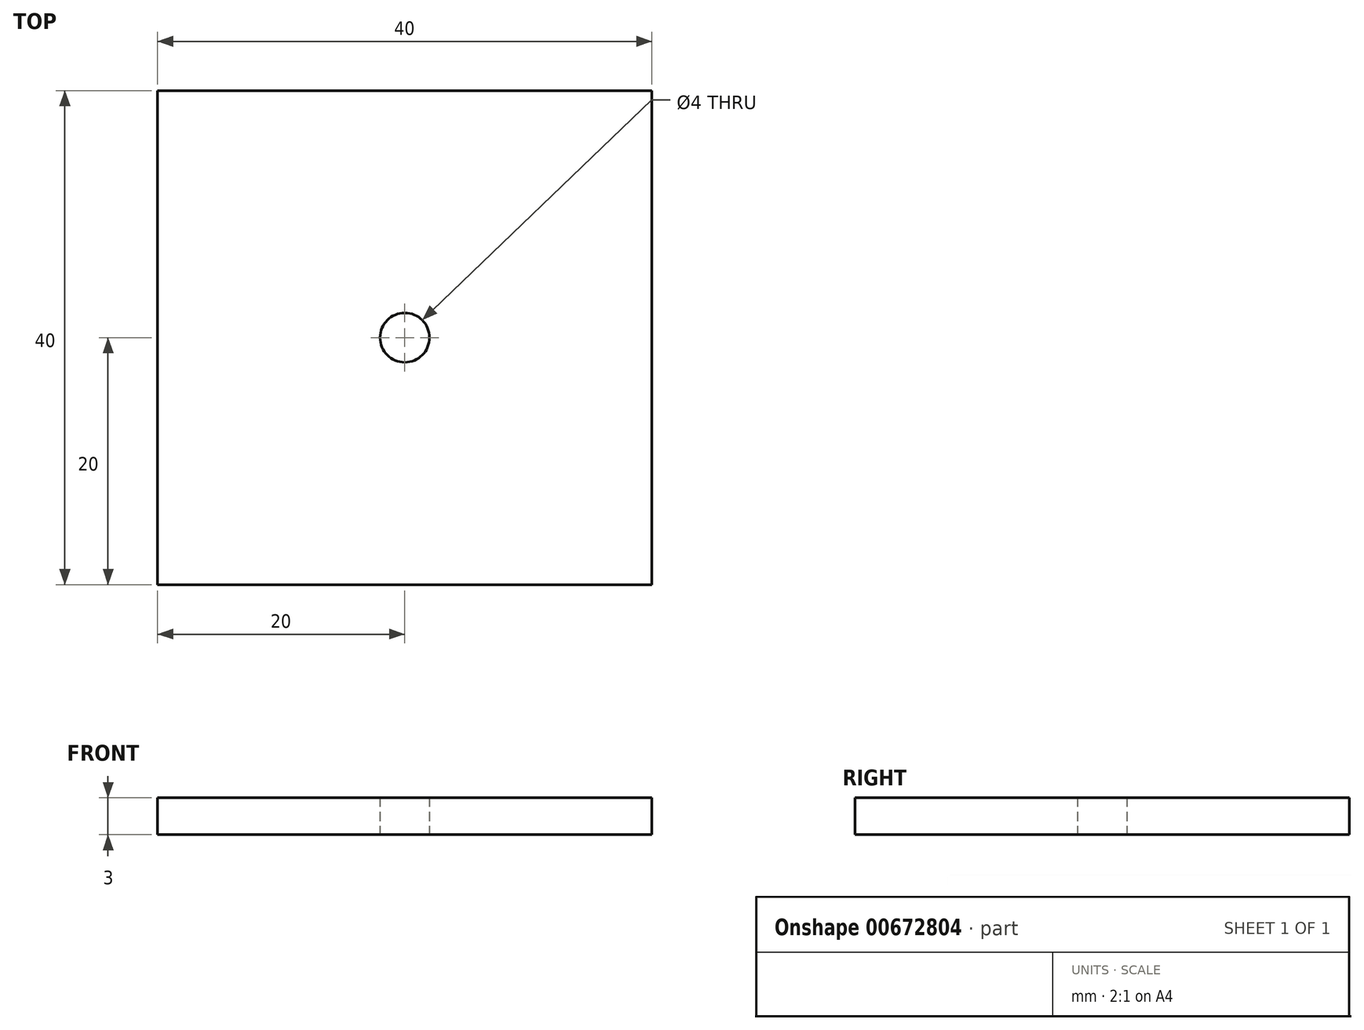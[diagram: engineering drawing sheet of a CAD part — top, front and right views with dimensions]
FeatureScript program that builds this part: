
annotation { "Feature Type Name" : "Feature", "Feature Type Description" : "" }
export const myFeature = defineFeature(function(context is Context, id is Id, definition is map)
    precondition{}
    {
        {
            var Q0;
            Q0=qCreatedBy(makeId("Top.planeOp"),FACE);
            var sketch = newSketch(context, id + "F0", { "sketchPlane" : qUnion([Q0])});
            skLineSegment(sketch, "E0.bottom", {"start": v(-20, 20) * mm, "end": v(20, 20) * mm});
            skLineSegment(sketch, "E0.top", {"start": v(-20, -20) * mm, "end": v(20, -20) * mm});
            skLineSegment(sketch, "E0.left", {"start": v(-20, 20) * mm, "end": v(-20, -20) * mm});
            skLineSegment(sketch, "E0.right", {"start": v(20, 20) * mm, "end": v(20, -20) * mm});
            skPoint(sketch, "E0.middle", {"position": v(0, 0) * mm});
            skCircle(sketch, "E1", {"center": v(0, 0) * mm, "radius": 2 * mm});
            skSolve(sketch);
        }
        {
            var Q0;
            Q0=makeQuery(id+"F0.imprint","IMPRINT",FACE,{"disambiguationData":[TD([[makeQuery(id+"F0.imprint","IMPRINT",EDGE,{"derivedFrom":sQuery(id+"F0.wireOp",EDGE,"E0.bottom")}),-1.0]])]});
            extrude(context, id + "F1", {"entities" : qUnion([Q0]), "depth" : 3 * mm, "offsetDistance" : 25 * mm});
        }
    });
